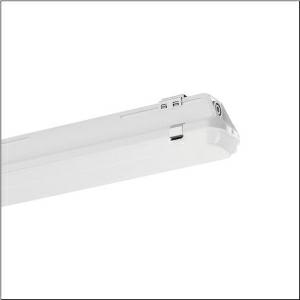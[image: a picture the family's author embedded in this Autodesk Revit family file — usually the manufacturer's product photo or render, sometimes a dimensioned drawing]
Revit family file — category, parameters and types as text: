
# Revit family: monsun_r__12_51fp12mp480h_818a
name_source: partatom
category: Lighting Fixtures
units: mm (PartAtom-declared; Revit-internal decimal feet)

## family parameters
Cut with Voids When Loaded = No
Host = Face
Light Source = No
Part Type = Normal
Room Calculation Point = No
Round Connector Dimension = Use Diameter
Shared = No

## types (1)
- --- (1 x LED, 7990 lm, 45.4 W, 4000K)
    Apparent Load = 45 VA
    CIE Flux Codes = 65 88 97 97 100
    Color Rendering = 80
    Color Temperature = 4000K
    Default Elevation = 1800 mm
    Description = Monsun® 12, damp-proof luminaire, chain hanger, primary light control with lens, primary optical cover: enclosure, of PMMA, light emission: direct distribution, primary light characteristic: symmetric, installation type: suspended mounting, surface-mounted, horizontal mounting, vertical mounting, LED rated luminous flux: 7.990 lm, light colour: 840, colour temperature: 4000K, control gear: ECG, with terminal, 3-pole, max. 2.5mm², mains connection: 220..240V, AC, 50/60Hz, rated input power: 45W, luminaire housing, of glass-fibre reinforced polyester, uncoated, bright grey, length: 1.590 mm, width: 90 mm, height: 88mm, clip for enclosure, of stainless steel (V2A), ceiling mounting element, of stainless steel (V2A), chain hanger, of stainless steel (V2A), protection rating (complete): IP66, insulation class (complete): insulation class I (protective earthing), certification: CE, ENEC, VDE, protection symbol: D, impact resistance: IK04, permissible ambient temperature for indoor applications: -35..+40°C, standard: EN 50419, EN 60598-2-1, no direct snow, no direct sun, no direct rain, for indoor or canopied outdoor use, corresponds to IFS (International Featured Standards) requirements for safety and quality in the food industry, for animal farming (ammonia tested): for use in cowhouse, pig house, horse-stables... (not for use in poultry stables), AT max for animal farming = 40°C, packaging unit: 1 piece
    Height = 89 mm
    Lamp = 1 x LED
    Lamp Light Flux = 7990 lm
    Lamp Power = 45.4 W
    Lamp count = 1
    Length = 1590 mm
    Luminous efficacy = 176 lm/W
    Manufacturer = Siteco
    ModVariant = No
    Model = 51FP12MP480H
    Mounting Place = Ceiling
    Mounting Type = Pendant
    Number of Poles = 1
    OnlyDefault = Yes
    Power Factor = 1
    Product Name = Monsun® 12
    Product group = damp-proof luminaire | ceiling pendant
    ProductGroupID = 908
    Protection Class = Protection class I
    Protection Degree = IP 66
    RLX_Detail_Level = 1
    RlxData = <blob elided: 90257 chars, md5=0e92bb32>
    Socket = socket
    Standby Power = 0 W
    System Light Flux = 7990 lm
    System Power = 45 W
    Type Comments = factory setting: luminous flux: 100 % | (A | C | E) | 105 mA
    Type Image = l_1004748.jpg
    URL = http://relux.com
    VarID = @adj_136097
    Voltage = 0 V
    Weight = 0.00 kg
    Width = 90 mm

## geometry (parser evidence)
native form markers: Blend x4, Sweep x10
no freeform markers — native parametric forms only
